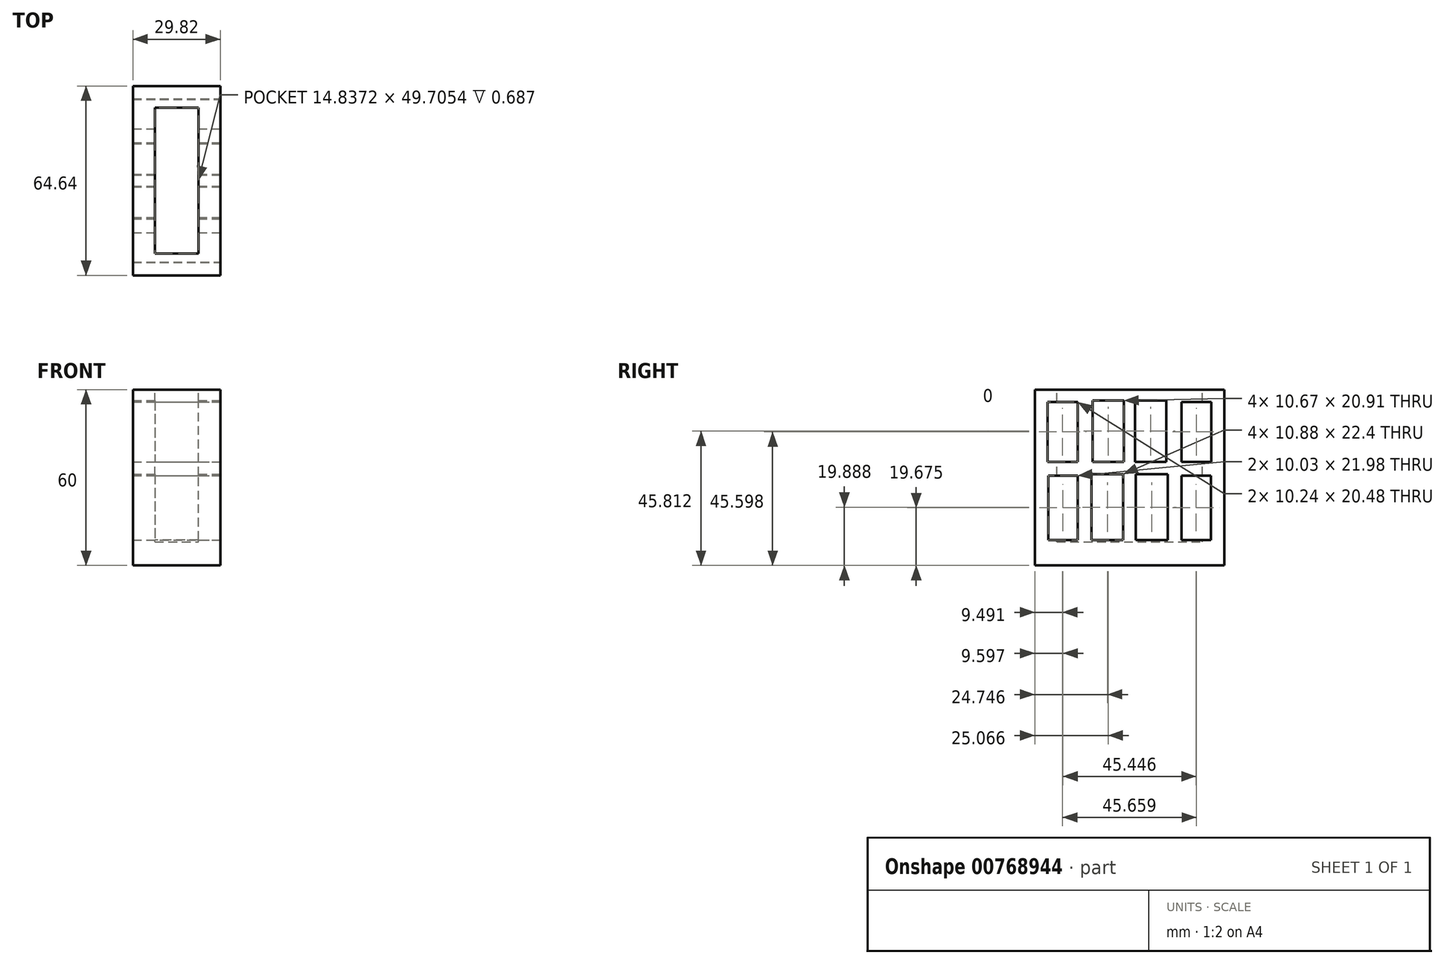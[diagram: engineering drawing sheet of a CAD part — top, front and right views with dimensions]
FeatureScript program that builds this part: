
annotation { "Feature Type Name" : "Feature", "Feature Type Description" : "" }
export const myFeature = defineFeature(function(context is Context, id is Id, definition is map)
    precondition{}
    {
        {
            var Q0;
            Q0=qCreatedBy(makeId("Top.planeOp"),FACE);
            var sketch = newSketch(context, id + "F0", { "sketchPlane" : qUnion([Q0])});
            skLineSegment(sketch, "E0.top", {"start": v(-0.07, 24.85) * mm, "end": v(7.42, 24.85) * mm});
            skLineSegment(sketch, "E0.right", {"start": v(7.42, 0) * mm, "end": v(7.42, 24.85) * mm});
            skLineSegment(sketch, "E1.MirrorCS", {"start": v(-7.42, 0) * mm, "end": v(-7.42, 24.85) * mm});
            skLineSegment(sketch, "E2.MirrorCS", {"start": v(0.07, 24.85) * mm, "end": v(-7.42, 24.85) * mm});
            skPoint(sketch, "E3.middle", {"position": v(0, 0) * mm});
            skLineSegment(sketch, "E4", {"start": v(-14.91, 24.85) * mm, "end": v(-14.91, 32.32) * mm});
            skLineSegment(sketch, "E5", {"start": v(-14.91, 32.32) * mm, "end": v(-7.42, 32.35) * mm});
            skLineSegment(sketch, "E6.MirrorCS", {"start": v(14.91, 24.85) * mm, "end": v(14.91, 32.32) * mm});
            skLineSegment(sketch, "E7.MirrorCS", {"start": v(14.91, 32.32) * mm, "end": v(7.42, 32.35) * mm});
            skLineSegment(sketch, "E8.MirrorCS", {"start": v(-14.91, -32.32) * mm, "end": v(-7.42, -32.35) * mm});
            skLineSegment(sketch, "E9.MirrorCS", {"start": v(-14.91, -24.85) * mm, "end": v(-14.91, -32.32) * mm});
            skLineSegment(sketch, "E10.MirrorCS", {"start": v(14.91, -24.85) * mm, "end": v(14.91, -32.32) * mm});
            skLineSegment(sketch, "E11.MirrorCS", {"start": v(14.91, -32.32) * mm, "end": v(7.42, -32.35) * mm});
            skLineSegment(sketch, "E12.bottom", {"start": v(-14.91, 32.32) * mm, "end": v(14.91, 32.32) * mm});
            skLineSegment(sketch, "E12.top", {"start": v(-14.91, -32.32) * mm, "end": v(14.91, -32.32) * mm});
            skLineSegment(sketch, "E12.left", {"start": v(-14.91, 32.32) * mm, "end": v(-14.91, -32.32) * mm});
            skLineSegment(sketch, "E12.right", {"start": v(14.91, 32.32) * mm, "end": v(14.91, -32.32) * mm});
            skLineSegment(sketch, "E13", {"start": v(7.42, 0) * mm, "end": v(7.42, -24.85) * mm});
            skLineSegment(sketch, "E14", {"start": v(-7.42, -24.85) * mm, "end": v(7.42, -24.85) * mm});
            skLineSegment(sketch, "E15", {"start": v(-7.42, -24.85) * mm, "end": v(-7.42, 0) * mm});
            skSolve(sketch);
        }
        {
            var Q0;
            Q0=makeQuery(id+"F0.imprint","IMPRINT",FACE,{"disambiguationData":[TD([[makeQuery(id+"F0.imprint","IMPRINT",EDGE,{"derivedFrom":sQuery(id+"F0.wireOp",EDGE,"E0.top")}),-1.0]])]});
            var sketch = newSketch(context, id + "F1", { "sketchPlane" : qUnion([Q0])});
            skLineSegment(sketch, "E16", {"start": v(0, 0) * mm, "end": v(-25, 0) * mm});
            skLineSegment(sketch, "E17", {"start": v(-25, 0) * mm, "end": v(-25, -50) * mm});
            skLineSegment(sketch, "E18", {"start": v(-25, -50) * mm, "end": v(0, -50) * mm});
            skLineSegment(sketch, "E19.MirrorCS", {"start": v(-25, 50) * mm, "end": v(-25, 0) * mm});
            skLineSegment(sketch, "E20.MirrorCS", {"start": v(0, 50) * mm, "end": v(-25, 50) * mm});
            skLineSegment(sketch, "E21", {"start": v(-25, 0) * mm, "end": v(-25, 0) * mm});
            skSolve(sketch);
        }
        {
            var Q0;
            Q0 = qSketchRegion(id + "F0", true);
            var Q1;
            {var subQ1=sQuery(id+"F0.wireOp",EDGE,"E0.top");Q1=makeQuery(id+"F0.imprint","IMPRINT",FACE,{"disambiguationData":[TD([[makeQuery(id+"F0.imprint","IMPRINT",EDGE,{"derivedFrom":subQ1}),-1.0]])]});}
            extrude(context, id + "F2", {"entities" : qUnion([Q0, Q1]), "oppositeDirection" : true, "depth" : 60 * mm, "offsetDistance" : 25.4 * mm});
        }
        {
            var Q0;
            {var subQ1=sQuery(id+"F0.wireOp",EDGE,"E0.top");Q0=makeQuery(id+"F1.imprint","IMPRINT",FACE,{"disambiguationData":[TD([[makeQuery(id+"F1.imprint","IMPRINT",EDGE,{"derivedFrom":makeQuery(id+"F0.imprint","IMPRINT",EDGE,{"derivedFrom":subQ1})}),-1.0]])]});}
            extrude(context, id + "F3", {"entities" : qUnion([Q0]), "operationType" : NewBodyOperationType.REMOVE, "oppositeDirection" : true, "depth" : 52 * mm, "offsetDistance" : 25.4 * mm});
        }
        {
            var Q0;
            Q0=makeQuery(id+"F2.opExtrude","SWEPT_FACE",FACE,{"disambiguationData":[OSD([sQuery(id+"F0.wireOp",EDGE,"E12.right")])]});
            var sketch = newSketch(context, id + "F4", { "sketchPlane" : qUnion([Q0])});
            skLineSegment(sketch, "E22.bottom", {"start": v(-27.95, -4.16) * mm, "end": v(-17.7, -4.16) * mm});
            skLineSegment(sketch, "E22.top", {"start": v(-27.95, -24.64) * mm, "end": v(-17.7, -24.64) * mm});
            skLineSegment(sketch, "E22.left", {"start": v(-27.95, -4.16) * mm, "end": v(-27.95, -24.64) * mm});
            skLineSegment(sketch, "E22.right", {"start": v(-17.7, -4.16) * mm, "end": v(-17.7, -24.64) * mm});
            skLineSegment(sketch, "E23.bottom", {"start": v(-27.74, -29.34) * mm, "end": v(-17.7, -29.34) * mm});
            skLineSegment(sketch, "E23.top", {"start": v(-27.74, -51.31) * mm, "end": v(-17.7, -51.31) * mm});
            skLineSegment(sketch, "E23.left", {"start": v(-27.74, -29.34) * mm, "end": v(-27.74, -51.31) * mm});
            skLineSegment(sketch, "E23.right", {"start": v(-17.7, -29.34) * mm, "end": v(-17.7, -51.31) * mm});
            skLineSegment(sketch, "E24.bottom", {"start": v(-12.59, -3.73) * mm, "end": v(-1.92, -3.73) * mm});
            skLineSegment(sketch, "E24.top", {"start": v(-12.59, -24.64) * mm, "end": v(-1.92, -24.64) * mm});
            skLineSegment(sketch, "E24.left", {"start": v(-12.59, -3.73) * mm, "end": v(-12.59, -24.64) * mm});
            skLineSegment(sketch, "E24.right", {"start": v(-1.92, -3.73) * mm, "end": v(-1.92, -24.64) * mm});
            skLineSegment(sketch, "E25.bottom", {"start": v(-13.01, -28.91) * mm, "end": v(-2.13, -28.91) * mm});
            skLineSegment(sketch, "E25.top", {"start": v(-13.01, -51.31) * mm, "end": v(-2.13, -51.31) * mm});
            skLineSegment(sketch, "E25.left", {"start": v(-13.01, -28.91) * mm, "end": v(-13.01, -51.31) * mm});
            skLineSegment(sketch, "E25.right", {"start": v(-2.13, -28.91) * mm, "end": v(-2.13, -51.31) * mm});
            skLineSegment(sketch, "E26.MirrorCS", {"start": v(1.92, -3.73) * mm, "end": v(1.92, -24.64) * mm});
            skLineSegment(sketch, "E27.MirrorCS", {"start": v(12.59, -3.73) * mm, "end": v(12.59, -24.64) * mm});
            skLineSegment(sketch, "E28.MirrorCS", {"start": v(12.59, -3.73) * mm, "end": v(1.92, -3.73) * mm});
            skLineSegment(sketch, "E29.MirrorCS", {"start": v(12.59, -24.64) * mm, "end": v(1.92, -24.64) * mm});
            skLineSegment(sketch, "E30.MirrorCS", {"start": v(13.01, -28.91) * mm, "end": v(2.13, -28.91) * mm});
            skLineSegment(sketch, "E31.MirrorCS", {"start": v(2.13, -28.91) * mm, "end": v(2.13, -51.31) * mm});
            skLineSegment(sketch, "E32.MirrorCS", {"start": v(13.01, -51.31) * mm, "end": v(2.13, -51.31) * mm});
            skLineSegment(sketch, "E33.MirrorCS", {"start": v(13.01, -28.91) * mm, "end": v(13.01, -51.31) * mm});
            skLineSegment(sketch, "E34.MirrorCS", {"start": v(17.7, -29.34) * mm, "end": v(17.7, -51.31) * mm});
            skLineSegment(sketch, "E35.MirrorCS", {"start": v(27.74, -29.34) * mm, "end": v(27.74, -51.31) * mm});
            skLineSegment(sketch, "E36.MirrorCS", {"start": v(27.74, -29.34) * mm, "end": v(17.7, -29.34) * mm});
            skLineSegment(sketch, "E37.MirrorCS", {"start": v(27.74, -51.31) * mm, "end": v(17.7, -51.31) * mm});
            skLineSegment(sketch, "E38.MirrorCS", {"start": v(27.95, -24.64) * mm, "end": v(17.7, -24.64) * mm});
            skLineSegment(sketch, "E39.MirrorCS", {"start": v(17.7, -4.16) * mm, "end": v(17.7, -24.64) * mm});
            skLineSegment(sketch, "E40.MirrorCS", {"start": v(27.95, -4.16) * mm, "end": v(27.95, -24.64) * mm});
            skLineSegment(sketch, "E41.MirrorCS", {"start": v(27.95, -4.16) * mm, "end": v(17.7, -4.16) * mm});
            skSolve(sketch);
        }
        {
            var Q0;
            Q0=makeQuery(id+"F4.imprint","IMPRINT",FACE,{"disambiguationData":[TD([[makeQuery(id+"F4.imprint","IMPRINT",EDGE,{"derivedFrom":sQuery(id+"F4.wireOp",EDGE,"E22.bottom")}),-1.0]])]});
            var Q1;
            Q1=makeQuery(id+"F4.imprint","IMPRINT",FACE,{"disambiguationData":[TD([[makeQuery(id+"F4.imprint","IMPRINT",EDGE,{"derivedFrom":sQuery(id+"F4.wireOp",EDGE,"E24.bottom")}),-1.0]])]});
            var Q2;
            Q2=makeQuery(id+"F4.imprint","IMPRINT",FACE,{"disambiguationData":[TD([[makeQuery(id+"F4.imprint","IMPRINT",EDGE,{"derivedFrom":sQuery(id+"F4.wireOp",EDGE,"E26.MirrorCS")}),1.0]])]});
            var Q3;
            Q3=makeQuery(id+"F4.imprint","IMPRINT",FACE,{"disambiguationData":[TD([[makeQuery(id+"F4.imprint","IMPRINT",EDGE,{"derivedFrom":sQuery(id+"F4.wireOp",EDGE,"E38.MirrorCS")}),-1.0]])]});
            var Q4;
            Q4=makeQuery(id+"F4.imprint","IMPRINT",FACE,{"disambiguationData":[TD([[makeQuery(id+"F4.imprint","IMPRINT",EDGE,{"derivedFrom":sQuery(id+"F4.wireOp",EDGE,"E34.MirrorCS")}),1.0]])]});
            var Q5;
            Q5=makeQuery(id+"F4.imprint","IMPRINT",FACE,{"disambiguationData":[TD([[makeQuery(id+"F4.imprint","IMPRINT",EDGE,{"derivedFrom":sQuery(id+"F4.wireOp",EDGE,"E30.MirrorCS")}),1.0]])]});
            var Q6;
            Q6=makeQuery(id+"F4.imprint","IMPRINT",FACE,{"disambiguationData":[TD([[makeQuery(id+"F4.imprint","IMPRINT",EDGE,{"derivedFrom":sQuery(id+"F4.wireOp",EDGE,"E25.bottom")}),-1.0]])]});
            var Q7;
            Q7=makeQuery(id+"F4.imprint","IMPRINT",FACE,{"disambiguationData":[TD([[makeQuery(id+"F4.imprint","IMPRINT",EDGE,{"derivedFrom":sQuery(id+"F4.wireOp",EDGE,"E23.bottom")}),-1.0]])]});
            extrude(context, id + "F5", {"entities" : qUnion([Q0, Q1, Q2, Q3, Q4, Q5, Q6, Q7]), "operationType" : NewBodyOperationType.REMOVE, "endBound" : BoundingType.THROUGH_ALL, "oppositeDirection" : true, "depth" : 25.4 * mm, "offsetDistance" : 25.4 * mm});
        }
        {
            var Q0;
            Q0=makeQuery(id+"F2.opExtrude","SWEPT_FACE",FACE,{"disambiguationData":[OSD([sQuery(id+"F0.wireOp",EDGE,"E12.left")])]});
            var sketch = newSketch(context, id + "F6", { "sketchPlane" : qUnion([Q0])});
            skLineSegment(sketch, "E42.bottom", {"start": v(-12.37, 0) * mm, "end": v(12.59, 0) * mm});
            skLineSegment(sketch, "E42.top", {"start": v(-12.37, -24.64) * mm, "end": v(12.59, -24.64) * mm});
            skLineSegment(sketch, "E42.left", {"start": v(-12.37, 0) * mm, "end": v(-12.37, -24.64) * mm});
            skLineSegment(sketch, "E42.right", {"start": v(12.59, 0) * mm, "end": v(12.59, -24.64) * mm});
            skSolve(sketch);
        }
        {
            var Q0;
            {var subQ0=sQuery(id+"F6.wireOp",EDGE,"E42.bottom");Q0=makeQuery(id+"F6.imprint","IMPRINT",FACE,{"disambiguationData":[TD([[makeQuery(id+"F6.imprint","IMPRINT",EDGE,{"derivedFrom":subQ0}),-1.0]])]});}
            var Q1;
            {var subQ0=sQuery(id+"F6.wireOp",EDGE,"E42.left");var subQ1=sQuery(id+"F6.wireOp",EDGE,"E42.top");var subQ2=makeQuery(id+"F6.imprint","INTERSECT",VERTEX,{"derivedFrom":[subQ1,subQ0]});Q1=makeQuery(id+"F6.imprint","IMPRINT",FACE,{"disambiguationData":[TD([[makeQuery(id+"F6.imprint","IMPRINT",EDGE,{"disambiguationData":[TD([[subQ2,-1.0]])],"derivedFrom":subQ1}),1.0]])]});}
            var Q2;
            {var subQ0=sQuery(id+"F6.wireOp",EDGE,"E42.right");var subQ1=sQuery(id+"F6.wireOp",EDGE,"E42.top");var subQ2=makeQuery(id+"F6.imprint","INTERSECT",VERTEX,{"derivedFrom":[subQ1,subQ0]});Q2=makeQuery(id+"F6.imprint","IMPRINT",FACE,{"disambiguationData":[TD([[makeQuery(id+"F6.imprint","IMPRINT",EDGE,{"disambiguationData":[TD([[subQ2,1.0]])],"derivedFrom":subQ1}),1.0]])]});}
            var Q3;
            {var subQ0=sQuery(id+"F6.wireOp",EDGE,"E42.left");var subQ1=sQuery(id+"F0.wireOp",EDGE,"E12.left");var subQ2=makeQuery(id+"F2.opExtrude","CAP_EDGE",EDGE,{"disambiguationData":[OSD([subQ1])],"isStart":true});var subQ3=makeQuery(id+"F6.imprint","INTERSECT",VERTEX,{"derivedFrom":[subQ2,subQ0]});Q3=makeQuery(id+"F6.imprint","IMPRINT",FACE,{"disambiguationData":[TD([[makeQuery(id+"F6.imprint","IMPRINT",EDGE,{"disambiguationData":[TD([[subQ3,-1.0]])],"derivedFrom":subQ2}),-1.0]])]});}
            extrude(context, id + "F7", {"entities" : qUnion([Q0, Q1, Q2, Q3]), "operationType" : NewBodyOperationType.REMOVE, "endBound" : BoundingType.THROUGH_ALL, "oppositeDirection" : true, "depth" : 25.4 * mm, "offsetDistance" : 25.4 * mm});
        }
    });
